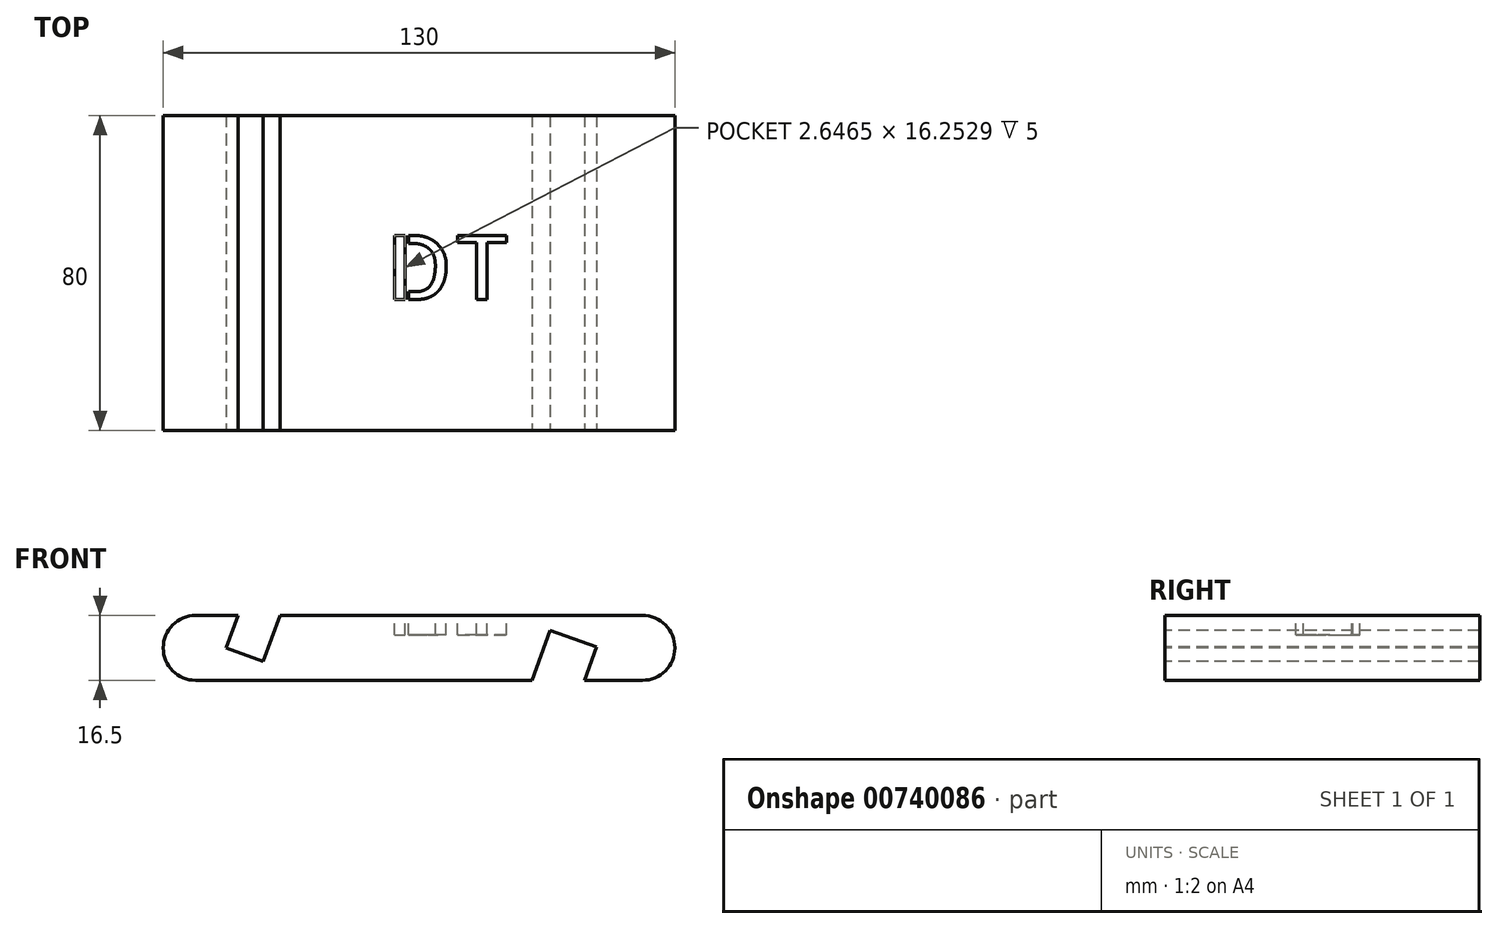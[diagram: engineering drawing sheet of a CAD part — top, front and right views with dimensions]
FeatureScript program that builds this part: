
annotation { "Feature Type Name" : "Feature", "Feature Type Description" : "" }
export const myFeature = defineFeature(function(context is Context, id is Id, definition is map)
    precondition{}
    {
        {
            var Q0;
            Q0=qCreatedBy(makeId("Top.planeOp"),FACE);
            var sketch = newSketch(context, id + "F0", { "sketchPlane" : qUnion([Q0])});
            skLineSegment(sketch, "E0.bottom", {"start": v(-66.26, 26.06) * mm, "end": v(63.74, 26.06) * mm});
            skLineSegment(sketch, "E0.top", {"start": v(-66.26, -53.94) * mm, "end": v(63.74, -53.94) * mm});
            skLineSegment(sketch, "E0.left", {"start": v(-66.26, 26.06) * mm, "end": v(-66.26, -53.94) * mm});
            skLineSegment(sketch, "E0.right", {"start": v(63.74, 26.06) * mm, "end": v(63.74, -53.94) * mm});
            skSolve(sketch);
        }
        {
            var Q0;
            Q0 = qSketchRegion(id + "F0", true);
            extrude(context, id + "F1", {"entities" : qUnion([Q0]), "depth" : 16.5 * mm, "offsetDistance" : 25 * mm});
        }
        {
            var Q0;
            Q0=makeQuery(id+"F1.opExtrude","CAP_EDGE",EDGE,{"disambiguationData":[OSD([sQuery(id+"F0.wireOp",EDGE,"E0.right")])],"isStart":false});
            var Q1;
            Q1=makeQuery(id+"F1.opExtrude","CAP_EDGE",EDGE,{"disambiguationData":[OSD([sQuery(id+"F0.wireOp",EDGE,"E0.right")])],"isStart":true});
            var Q2;
            Q2=makeQuery(id+"F1.opExtrude","CAP_EDGE",EDGE,{"disambiguationData":[OSD([sQuery(id+"F0.wireOp",EDGE,"E0.left")])],"isStart":false});
            var Q3;
            Q3=makeQuery(id+"F1.opExtrude","CAP_EDGE",EDGE,{"disambiguationData":[OSD([sQuery(id+"F0.wireOp",EDGE,"E0.left")])],"isStart":true});
            fillet(context, id + "F2", {"entities" : qUnion([Q0, Q1, Q2, Q3]), "radius" : 8.25 * mm, "tangentPropagation" : true, "allowEdgeOverflow" : false});
        }
        {
            var Q0;
            Q0=makeQuery(id+"F1.opExtrude","SWEPT_FACE",FACE,{"disambiguationData":[OSD([sQuery(id+"F0.wireOp",EDGE,"E0.top")])]});
            var sketch = newSketch(context, id + "F3", { "sketchPlane" : qUnion([Q0])});
            skPoint(sketch, "E1", {"position": v(-47.26, 16.5) * mm});
            skLineSegment(sketch, "E2", {"start": v(-47.26, 16.5) * mm, "end": v(-50.27, 8.23) * mm});
            skLineSegment(sketch, "E3", {"start": v(-50.27, 8.23) * mm, "end": v(-40.87, 4.81) * mm});
            skPoint(sketch, "E4", {"position": v(40.74, 0) * mm});
            skLineSegment(sketch, "E5", {"start": v(43.82, 8.46) * mm, "end": v(40.74, 0) * mm});
            skLineSegment(sketch, "E6", {"start": v(-40.87, 4.81) * mm, "end": v(-36.62, 16.5) * mm});
            skLineSegment(sketch, "E7", {"start": v(43.82, 8.46) * mm, "end": v(32.07, 12.73) * mm});
            skLineSegment(sketch, "E8", {"start": v(32.07, 12.73) * mm, "end": v(27.44, 0) * mm});
            skSolve(sketch);
        }
        {
            var Q0;
            {var subQ0=sQuery(id+"F3.wireOp",EDGE,"E2");Q0=makeQuery(id+"F3.imprint","IMPRINT",FACE,{"disambiguationData":[TD([[makeQuery(id+"F3.imprint","IMPRINT",EDGE,{"derivedFrom":subQ0}),1.0]])]});}
            var Q1;
            {var subQ0=sQuery(id+"F3.wireOp",EDGE,"E5");Q1=makeQuery(id+"F3.imprint","IMPRINT",FACE,{"disambiguationData":[TD([[makeQuery(id+"F3.imprint","IMPRINT",EDGE,{"derivedFrom":subQ0}),-1.0]])]});}
            extrude(context, id + "F4", {"entities" : qUnion([Q0, Q1]), "operationType" : NewBodyOperationType.REMOVE, "endBound" : BoundingType.UP_TO_NEXT, "oppositeDirection" : true, "depth" : 25 * mm, "offsetDistance" : 25 * mm});
        }
        {
            var Q0;
            {var subQ0=sQuery(id+"F0.wireOp",EDGE,"E0.bottom");var subQ1=sQuery(id+"F0.wireOp",EDGE,"E0.top");var subQ2=sQuery(id+"F0.wireOp",EDGE,"E0.right");Q0=makeQuery(id+"F4.boolean.opBoolean","SPLIT",FACE,{"disambiguationData":[TD([makeQuery(id+"F2.opFillet","BLEND_FACE",FACE,{"disambiguationData":[OSD([subQ2])]})])],"derivedFrom":makeQuery(id+"F1.opExtrude","CAP_FACE",FACE,{"disambiguationData":[OSD([subQ0,subQ1,sQuery(id+"F0.wireOp",EDGE,"E0.left"),subQ2])],"isStart":false})});}
            var sketch = newSketch(context, id + "F5", { "sketchPlane" : qUnion([Q0])});
            skText(sketch, "E9", { "text": "DT", "fontName": "AllertaStencil-Regular.ttf"});
            const initialGuessF5  = {"E9": [-0.00957, -0.02065, 1, 0, 0.01626]};
            skSetInitialGuess(sketch, initialGuessF5);
            skSolve(sketch);
        }
        {
            var Q0;
            Q0 = qSketchRegion(id + "F5", true);
            extrude(context, id + "F6", {"entities" : qUnion([Q0]), "operationType" : NewBodyOperationType.REMOVE, "oppositeDirection" : true, "depth" : 5 * mm, "offsetDistance" : 25 * mm});
        }
    });
